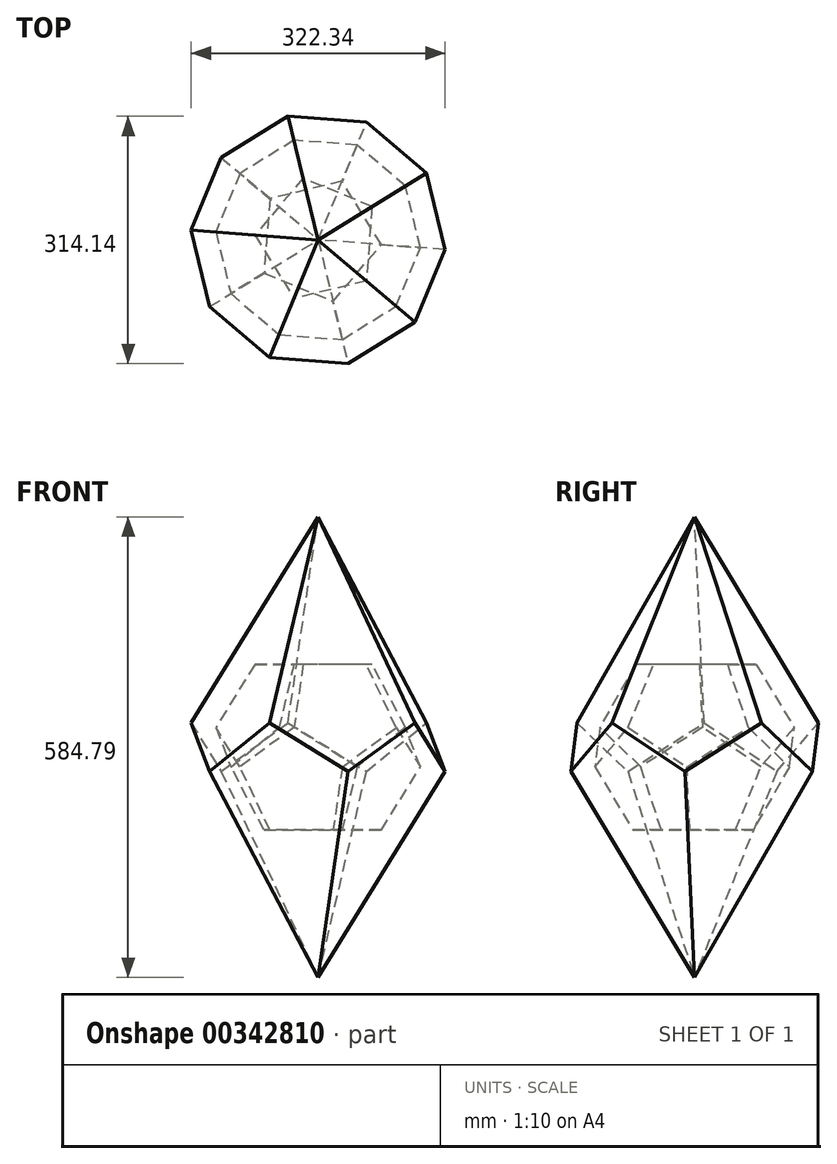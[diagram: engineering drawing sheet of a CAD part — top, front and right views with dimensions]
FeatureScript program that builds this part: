
annotation { "Feature Type Name" : "Feature", "Feature Type Description" : "" }
export const myFeature = defineFeature(function(context is Context, id is Id, definition is map)
    precondition{}
    {
        {
            var Q0;
            Q0=qCreatedBy(makeId("Top.planeOp"),FACE);
            var sketch = newSketch(context, id + "F0", { "sketchPlane" : qUnion([Q0])});
            skCircle(sketch, "E0.cCircle", {"center": v(0, 0) * mm, "radius": 80.82 * mm, "construction": true});
            skLineSegment(sketch, "E0.0", {"start": v(99.6, -7.58) * mm, "end": v(23.57, -97.07) * mm});
            skLineSegment(sketch, "E0.1", {"start": v(23.57, -97.07) * mm, "end": v(-85.04, -52.42) * mm});
            skLineSegment(sketch, "E0.2", {"start": v(-85.04, -52.42) * mm, "end": v(-76.13, 64.68) * mm});
            skLineSegment(sketch, "E0.3", {"start": v(-76.13, 64.68) * mm, "end": v(37.99, 92.39) * mm});
            skLineSegment(sketch, "E0.4", {"start": v(37.99, 92.39) * mm, "end": v(99.6, -7.58) * mm});
            skPoint(sketch, "E0.0.midPoint", {"position": v(61.59, -52.33) * mm});
            skSolve(sketch);
        }
        {
            var Q0;
            Q0=makeQuery(id+"F0.imprint","IMPRINT",FACE,{"disambiguationData":[TD([[makeQuery(id+"F0.imprint","IMPRINT",EDGE,{"derivedFrom":sQuery(id+"F0.wireOp",EDGE,"E0.0")}),-1.0]])]});
            extrude(context, id + "F1", {"entities" : qUnion([Q0]), "depth" : 25.4 * mm});
        }
        {
            var Q0;
            Q0=makeQuery(id+"F1.opExtrude","CAP_EDGE",EDGE,{"disambiguationData":[OSD([sQuery(id+"F0.wireOp",EDGE,"E0.1")])],"isStart":false});
            var Q1;
            Q1=makeQuery(id+"F1.opExtrude","CAP_EDGE",EDGE,{"disambiguationData":[OSD([sQuery(id+"F0.wireOp",EDGE,"E0.2")])],"isStart":false});
            var Q2;
            Q2=makeQuery(id+"F1.opExtrude","CAP_EDGE",EDGE,{"disambiguationData":[OSD([sQuery(id+"F0.wireOp",EDGE,"E0.3")])],"isStart":false});
            var Q3;
            Q3=makeQuery(id+"F1.opExtrude","CAP_EDGE",EDGE,{"disambiguationData":[OSD([sQuery(id+"F0.wireOp",EDGE,"E0.4")])],"isStart":false});
            var Q4;
            Q4=makeQuery(id+"F1.opExtrude","CAP_EDGE",EDGE,{"disambiguationData":[OSD([sQuery(id+"F0.wireOp",EDGE,"E0.0")])],"isStart":false});
            chamfer(context, id + "F2", {"entities" : qUnion([Q0, Q1, Q2, Q3, Q4]), "chamferType" : ChamferType.OFFSET_ANGLE, "width" : 25.4 * mm, "oppositeDirection" : false, "angle" : 31.72 * degree, "tangentPropagation" : true});
        }
        {
            var Q0;
            Q0=makeQuery(id+"F1.opExtrude","SWEPT_BODY",BODY,{"disambiguationData":[OSD([sQuery(id+"F0.wireOp",EDGE,"E0.0"),sQuery(id+"F0.wireOp",EDGE,"E0.1"),sQuery(id+"F0.wireOp",EDGE,"E0.2"),sQuery(id+"F0.wireOp",EDGE,"E0.3"),sQuery(id+"F0.wireOp",EDGE,"E0.4")])]});
            var Q1;
            Q1=makeQuery(id+"F2.opChamfer","BLEND_EDGE",EDGE,{"blendedFrom":[makeQuery(id+"F1.opExtrude","CAP_EDGE",EDGE,{"disambiguationData":[OSD([sQuery(id+"F0.wireOp",EDGE,"E0.1")])],"isStart":false}),makeQuery(id+"F1.opExtrude","CAP_EDGE",EDGE,{"disambiguationData":[OSD([sQuery(id+"F0.wireOp",EDGE,"E0.2")])],"isStart":false})],"blendedInto":[]});
            circularPattern(context, id + "F3", {"entities" : qUnion([Q0]), "axis" : qUnion([Q1]), "angle" : 360 * degree, "instanceCount" : 3, "equalSpace" : true});
        }
        {
            var Q0;
            Q0=makeQuery(id+"F1.opExtrude","SWEPT_BODY",BODY,{"disambiguationData":[OSD([sQuery(id+"F0.wireOp",EDGE,"E0.0"),sQuery(id+"F0.wireOp",EDGE,"E0.1"),sQuery(id+"F0.wireOp",EDGE,"E0.2"),sQuery(id+"F0.wireOp",EDGE,"E0.3"),sQuery(id+"F0.wireOp",EDGE,"E0.4")])]});
            var Q1;
            Q1=makeQuery(id+"F3.opPattern","COPY",BODY,{"derivedFrom":makeQuery(id+"F1.opExtrude","SWEPT_BODY",BODY,{"disambiguationData":[OSD([sQuery(id+"F0.wireOp",EDGE,"E0.0"),sQuery(id+"F0.wireOp",EDGE,"E0.1"),sQuery(id+"F0.wireOp",EDGE,"E0.2"),sQuery(id+"F0.wireOp",EDGE,"E0.3"),sQuery(id+"F0.wireOp",EDGE,"E0.4")])]}),"instanceName":"1"});
            var Q2;
            Q2=makeQuery(id+"F3.opPattern","COPY",BODY,{"derivedFrom":makeQuery(id+"F1.opExtrude","SWEPT_BODY",BODY,{"disambiguationData":[OSD([sQuery(id+"F0.wireOp",EDGE,"E0.0"),sQuery(id+"F0.wireOp",EDGE,"E0.1"),sQuery(id+"F0.wireOp",EDGE,"E0.2"),sQuery(id+"F0.wireOp",EDGE,"E0.3"),sQuery(id+"F0.wireOp",EDGE,"E0.4")])]}),"instanceName":"2"});
            var Q3;
            Q3=makeQuery(id+"F2.opChamfer","BLEND_EDGE",EDGE,{"blendedFrom":[makeQuery(id+"F1.opExtrude","CAP_EDGE",EDGE,{"disambiguationData":[OSD([sQuery(id+"F0.wireOp",EDGE,"E0.0")])],"isStart":false}),makeQuery(id+"F1.opExtrude","CAP_EDGE",EDGE,{"disambiguationData":[OSD([sQuery(id+"F0.wireOp",EDGE,"E0.4")])],"isStart":false})],"blendedInto":[]});
            transform(context, id + "F4", {"entities" : qUnion([Q0, Q1, Q2]), "transformType" : TransformType.ROTATION, "transformAxis" : qUnion([Q3]), "angle" : 120 * degree, "makeCopy" : true});
        }
        {
            var Q0;
            Q0=makeQuery(id+"F4.opPattern","COPY",BODY,{"derivedFrom":makeQuery(id+"F3.opPattern","COPY",BODY,{"derivedFrom":makeQuery(id+"F1.opExtrude","SWEPT_BODY",BODY,{"disambiguationData":[OSD([sQuery(id+"F0.wireOp",EDGE,"E0.0"),sQuery(id+"F0.wireOp",EDGE,"E0.1"),sQuery(id+"F0.wireOp",EDGE,"E0.2"),sQuery(id+"F0.wireOp",EDGE,"E0.3"),sQuery(id+"F0.wireOp",EDGE,"E0.4")])]}),"instanceName":"1"}),"instanceName":"1"});
            var Q1;
            Q1=makeQuery(id+"F4.opPattern","COPY",BODY,{"derivedFrom":makeQuery(id+"F3.opPattern","COPY",BODY,{"derivedFrom":makeQuery(id+"F1.opExtrude","SWEPT_BODY",BODY,{"disambiguationData":[OSD([sQuery(id+"F0.wireOp",EDGE,"E0.0"),sQuery(id+"F0.wireOp",EDGE,"E0.1"),sQuery(id+"F0.wireOp",EDGE,"E0.2"),sQuery(id+"F0.wireOp",EDGE,"E0.3"),sQuery(id+"F0.wireOp",EDGE,"E0.4")])]}),"instanceName":"2"}),"instanceName":"1"});
            var Q2;
            Q2=makeQuery(id+"F4.opPattern","COPY",BODY,{"derivedFrom":makeQuery(id+"F1.opExtrude","SWEPT_BODY",BODY,{"disambiguationData":[OSD([sQuery(id+"F0.wireOp",EDGE,"E0.0"),sQuery(id+"F0.wireOp",EDGE,"E0.1"),sQuery(id+"F0.wireOp",EDGE,"E0.2"),sQuery(id+"F0.wireOp",EDGE,"E0.3"),sQuery(id+"F0.wireOp",EDGE,"E0.4")])]}),"instanceName":"1"});
            var Q3;
            Q3=makeQuery(id+"F4.opPattern","COPY",EDGE,{"derivedFrom":makeQuery(id+"F3.opPattern","COPY",EDGE,{"derivedFrom":makeQuery(id+"F2.opChamfer","BLEND_EDGE",EDGE,{"blendedFrom":[makeQuery(id+"F1.opExtrude","CAP_EDGE",EDGE,{"disambiguationData":[OSD([sQuery(id+"F0.wireOp",EDGE,"E0.0")])],"isStart":false}),makeQuery(id+"F1.opExtrude","CAP_EDGE",EDGE,{"disambiguationData":[OSD([sQuery(id+"F0.wireOp",EDGE,"E0.4")])],"isStart":false})],"blendedInto":[]}),"instanceName":"2"}),"instanceName":"1"});
            transform(context, id + "F5", {"entities" : qUnion([Q0, Q1, Q2]), "transformType" : TransformType.ROTATION, "transformAxis" : qUnion([Q3]), "angle" : 120 * degree, "makeCopy" : true});
        }
        {
            var Q0;
            Q0=makeQuery(id+"F5.opPattern","COPY",BODY,{"derivedFrom":makeQuery(id+"F4.opPattern","COPY",BODY,{"derivedFrom":makeQuery(id+"F1.opExtrude","SWEPT_BODY",BODY,{"disambiguationData":[OSD([sQuery(id+"F0.wireOp",EDGE,"E0.0"),sQuery(id+"F0.wireOp",EDGE,"E0.1"),sQuery(id+"F0.wireOp",EDGE,"E0.2"),sQuery(id+"F0.wireOp",EDGE,"E0.3"),sQuery(id+"F0.wireOp",EDGE,"E0.4")])]}),"instanceName":"1"}),"instanceName":"1"});
            var Q1;
            Q1=makeQuery(id+"F4.opPattern","COPY",BODY,{"derivedFrom":makeQuery(id+"F3.opPattern","COPY",BODY,{"derivedFrom":makeQuery(id+"F1.opExtrude","SWEPT_BODY",BODY,{"disambiguationData":[OSD([sQuery(id+"F0.wireOp",EDGE,"E0.0"),sQuery(id+"F0.wireOp",EDGE,"E0.1"),sQuery(id+"F0.wireOp",EDGE,"E0.2"),sQuery(id+"F0.wireOp",EDGE,"E0.3"),sQuery(id+"F0.wireOp",EDGE,"E0.4")])]}),"instanceName":"2"}),"instanceName":"1"});
            var Q2;
            Q2=makeQuery(id+"F5.opPattern","COPY",BODY,{"derivedFrom":makeQuery(id+"F4.opPattern","COPY",BODY,{"derivedFrom":makeQuery(id+"F3.opPattern","COPY",BODY,{"derivedFrom":makeQuery(id+"F1.opExtrude","SWEPT_BODY",BODY,{"disambiguationData":[OSD([sQuery(id+"F0.wireOp",EDGE,"E0.0"),sQuery(id+"F0.wireOp",EDGE,"E0.1"),sQuery(id+"F0.wireOp",EDGE,"E0.2"),sQuery(id+"F0.wireOp",EDGE,"E0.3"),sQuery(id+"F0.wireOp",EDGE,"E0.4")])]}),"instanceName":"2"}),"instanceName":"1"}),"instanceName":"1"});
            var Q3;
            Q3=makeQuery(id+"F5.opPattern","COPY",EDGE,{"derivedFrom":makeQuery(id+"F4.opPattern","COPY",EDGE,{"derivedFrom":makeQuery(id+"F3.opPattern","COPY",EDGE,{"derivedFrom":makeQuery(id+"F2.opChamfer","BLEND_EDGE",EDGE,{"blendedFrom":[makeQuery(id+"F1.opExtrude","CAP_EDGE",EDGE,{"disambiguationData":[OSD([sQuery(id+"F0.wireOp",EDGE,"E0.2")])],"isStart":false}),makeQuery(id+"F1.opExtrude","CAP_EDGE",EDGE,{"disambiguationData":[OSD([sQuery(id+"F0.wireOp",EDGE,"E0.3")])],"isStart":false})],"blendedInto":[]}),"instanceName":"2"}),"instanceName":"1"}),"instanceName":"1"});
            transform(context, id + "F6", {"entities" : qUnion([Q0, Q1, Q2]), "transformType" : TransformType.ROTATION, "transformAxis" : qUnion([Q3]), "angle" : 240 * degree, "makeCopy" : true});
        }
        {
            var Q0;
            Q0=makeQuery(id+"F6.opPattern","COPY",FACE,{"derivedFrom":makeQuery(id+"F5.opPattern","COPY",FACE,{"derivedFrom":makeQuery(id+"F4.opPattern","COPY",FACE,{"derivedFrom":makeQuery(id+"F3.opPattern","COPY",FACE,{"derivedFrom":makeQuery(id+"F1.opExtrude","CAP_FACE",FACE,{"disambiguationData":[OSD([sQuery(id+"F0.wireOp",EDGE,"E0.0"),sQuery(id+"F0.wireOp",EDGE,"E0.1"),sQuery(id+"F0.wireOp",EDGE,"E0.2"),sQuery(id+"F0.wireOp",EDGE,"E0.3"),sQuery(id+"F0.wireOp",EDGE,"E0.4")])],"isStart":true}),"instanceName":"2"}),"instanceName":"1"}),"instanceName":"1"}),"instanceName":"1"});
            var sketch = newSketch(context, id + "F7", { "sketchPlane" : qUnion([Q0])});
            skLineSegment(sketch, "E1", {"start": v(-103.74, 75.33) * mm, "end": v(-29.05, 432.82) * mm});
            skSolve(sketch);
        }
        {
            var Q0;
            Q0=makeQuery(id+"F6.opPattern","COPY",FACE,{"derivedFrom":makeQuery(id+"F5.opPattern","COPY",FACE,{"derivedFrom":makeQuery(id+"F4.opPattern","COPY",FACE,{"derivedFrom":makeQuery(id+"F1.opExtrude","CAP_FACE",FACE,{"disambiguationData":[OSD([sQuery(id+"F0.wireOp",EDGE,"E0.0"),sQuery(id+"F0.wireOp",EDGE,"E0.1"),sQuery(id+"F0.wireOp",EDGE,"E0.2"),sQuery(id+"F0.wireOp",EDGE,"E0.3"),sQuery(id+"F0.wireOp",EDGE,"E0.4")])],"isStart":true}),"instanceName":"1"}),"instanceName":"1"}),"instanceName":"1"});
            var sketch = newSketch(context, id + "F8", { "sketchPlane" : qUnion([Q0])});
            skLineSegment(sketch, "E2", {"start": v(97.88, 82.8) * mm, "end": v(-27.14, 517.31) * mm});
            skSolve(sketch);
        }
        {
            var Q0;
            {var subQ0=sQuery(id+"F0.wireOp",EDGE,"E0.4");var subQ1=sQuery(id+"F0.wireOp",EDGE,"E0.2");var subQ2=sQuery(id+"F0.wireOp",EDGE,"E0.1");var subQ3=sQuery(id+"F0.wireOp",EDGE,"E0.0");var subQ4=makeQuery(id+"F1.opExtrude","CAP_FACE",FACE,{"disambiguationData":[OSD([subQ3,subQ2,subQ1,sQuery(id+"F0.wireOp",EDGE,"E0.3"),subQ0])],"isStart":true});Q0=makeQuery(id+"F7.imprint","IMPRINT",FACE,{"disambiguationData":[TD([[makeQuery(id+"F7.imprint","IMPRINT",EDGE,{"derivedFrom":makeQuery(id+"F6.opPattern","COPY",EDGE,{"derivedFrom":makeQuery(id+"F5.opPattern","COPY",EDGE,{"derivedFrom":makeQuery(id+"F4.opPattern","COPY",EDGE,{"derivedFrom":makeQuery(id+"F3.opPattern","COPY",EDGE,{"derivedFrom":makeQuery(id+"F2.opChamfer","BLEND_EDGE",EDGE,{"blendedFrom":[makeQuery(id+"F1.opExtrude","CAP_EDGE",EDGE,{"disambiguationData":[OSD([subQ3])],"isStart":false}),subQ4],"blendedInto":[subQ4]}),"instanceName":"2"}),"instanceName":"1"}),"instanceName":"1"}),"instanceName":"1"})}),1.0]])]});}
            var sketch = newSketch(context, id + "F9", { "sketchPlane" : qUnion([Q0])});
            skLineSegment(sketch, "E3", {"start": v(-40.86, 376.27) * mm, "end": v(-0.97, 360.76) * mm});
            skSolve(sketch);
        }
        {
            var Q1;
            Q1=makeQuery(id+"F5.opPattern","COPY",FACE,{"derivedFrom":makeQuery(id+"F4.opPattern","COPY",FACE,{"derivedFrom":makeQuery(id+"F3.opPattern","COPY",FACE,{"derivedFrom":makeQuery(id+"F1.opExtrude","CAP_FACE",FACE,{"disambiguationData":[OSD([sQuery(id+"F0.wireOp",EDGE,"E0.0"),sQuery(id+"F0.wireOp",EDGE,"E0.1"),sQuery(id+"F0.wireOp",EDGE,"E0.2"),sQuery(id+"F0.wireOp",EDGE,"E0.3"),sQuery(id+"F0.wireOp",EDGE,"E0.4")])],"isStart":true}),"instanceName":"2"}),"instanceName":"1"}),"instanceName":"1"});
            var Q2;
            Q2=sQuery(id+"F9.wireOp",VERTEX,"E3.start");
            loft(context, id + "F10", {"operationType" : NewBodyOperationType.ADD, "sheetProfilesArray" : [{ "sheetProfileEntities" : qUnion([Q1]) }, { "sheetProfileEntities" : qUnion([Q2]) }]});
        }
        {
            var Q0;
            Q0=makeQuery(id+"F6.opPattern","COPY",FACE,{"derivedFrom":makeQuery(id+"F4.opPattern","COPY",FACE,{"derivedFrom":makeQuery(id+"F3.opPattern","COPY",FACE,{"derivedFrom":makeQuery(id+"F1.opExtrude","CAP_FACE",FACE,{"disambiguationData":[OSD([sQuery(id+"F0.wireOp",EDGE,"E0.0"),sQuery(id+"F0.wireOp",EDGE,"E0.1"),sQuery(id+"F0.wireOp",EDGE,"E0.2"),sQuery(id+"F0.wireOp",EDGE,"E0.3"),sQuery(id+"F0.wireOp",EDGE,"E0.4")])],"isStart":true}),"instanceName":"2"}),"instanceName":"1"}),"instanceName":"1"});
            var sketch = newSketch(context, id + "F11", { "sketchPlane" : qUnion([Q0])});
            skLineSegment(sketch, "E4", {"start": v(38.24, 132.45) * mm, "end": v(57.54, -261.56) * mm});
            skSolve(sketch);
        }
        {
            var Q0;
            Q0=makeQuery(id+"F3.opPattern","COPY",FACE,{"derivedFrom":makeQuery(id+"F1.opExtrude","CAP_FACE",FACE,{"disambiguationData":[OSD([sQuery(id+"F0.wireOp",EDGE,"E0.0"),sQuery(id+"F0.wireOp",EDGE,"E0.1"),sQuery(id+"F0.wireOp",EDGE,"E0.2"),sQuery(id+"F0.wireOp",EDGE,"E0.3"),sQuery(id+"F0.wireOp",EDGE,"E0.4")])],"isStart":true}),"instanceName":"1"});
            var sketch = newSketch(context, id + "F12", { "sketchPlane" : qUnion([Q0])});
            skLineSegment(sketch, "E5", {"start": v(63.3, 137.03) * mm, "end": v(11.57, -251.7) * mm});
            skLineSegment(sketch, "E6", {"start": v(-108.02, 105.75) * mm, "end": v(104.5, -286.97) * mm});
            skLineSegment(sketch, "E7", {"start": v(-9.37, -80.49) * mm, "end": v(26.14, -142.18) * mm});
            skSolve(sketch);
        }
        {
            var Q1;
            Q1=makeQuery(id+"F1.opExtrude","CAP_FACE",FACE,{"disambiguationData":[OSD([sQuery(id+"F0.wireOp",EDGE,"E0.0"),sQuery(id+"F0.wireOp",EDGE,"E0.1"),sQuery(id+"F0.wireOp",EDGE,"E0.2"),sQuery(id+"F0.wireOp",EDGE,"E0.3"),sQuery(id+"F0.wireOp",EDGE,"E0.4")])],"isStart":true});
            var Q2;
            Q2=sQuery(id+"F12.wireOp",VERTEX,"E7.end");
            loft(context, id + "F13", {"operationType" : NewBodyOperationType.ADD, "sheetProfilesArray" : [{ "sheetProfileEntities" : qUnion([Q1]) }, { "sheetProfileEntities" : qUnion([Q2]) }]});
        }
        {
            var Q0;
            Q0=makeQuery(id+"F1.opExtrude","SWEPT_BODY",BODY,{"disambiguationData":[OSD([sQuery(id+"F0.wireOp",EDGE,"E0.0"),sQuery(id+"F0.wireOp",EDGE,"E0.1"),sQuery(id+"F0.wireOp",EDGE,"E0.2"),sQuery(id+"F0.wireOp",EDGE,"E0.3"),sQuery(id+"F0.wireOp",EDGE,"E0.4")])]});
            var Q1;
            Q1=makeQuery(id+"F4.opPattern","COPY",BODY,{"derivedFrom":makeQuery(id+"F1.opExtrude","SWEPT_BODY",BODY,{"disambiguationData":[OSD([sQuery(id+"F0.wireOp",EDGE,"E0.0"),sQuery(id+"F0.wireOp",EDGE,"E0.1"),sQuery(id+"F0.wireOp",EDGE,"E0.2"),sQuery(id+"F0.wireOp",EDGE,"E0.3"),sQuery(id+"F0.wireOp",EDGE,"E0.4")])]}),"instanceName":"1"});
            var Q2;
            Q2=makeQuery(id+"F6.opPattern","COPY",BODY,{"derivedFrom":makeQuery(id+"F4.opPattern","COPY",BODY,{"derivedFrom":makeQuery(id+"F3.opPattern","COPY",BODY,{"derivedFrom":makeQuery(id+"F1.opExtrude","SWEPT_BODY",BODY,{"disambiguationData":[OSD([sQuery(id+"F0.wireOp",EDGE,"E0.0"),sQuery(id+"F0.wireOp",EDGE,"E0.1"),sQuery(id+"F0.wireOp",EDGE,"E0.2"),sQuery(id+"F0.wireOp",EDGE,"E0.3"),sQuery(id+"F0.wireOp",EDGE,"E0.4")])]}),"instanceName":"2"}),"instanceName":"1"}),"instanceName":"1"});
            var Q3;
            Q3=makeQuery(id+"F3.opPattern","COPY",BODY,{"derivedFrom":makeQuery(id+"F1.opExtrude","SWEPT_BODY",BODY,{"disambiguationData":[OSD([sQuery(id+"F0.wireOp",EDGE,"E0.0"),sQuery(id+"F0.wireOp",EDGE,"E0.1"),sQuery(id+"F0.wireOp",EDGE,"E0.2"),sQuery(id+"F0.wireOp",EDGE,"E0.3"),sQuery(id+"F0.wireOp",EDGE,"E0.4")])]}),"instanceName":"1"});
            var Q4;
            Q4=makeQuery(id+"F6.opPattern","COPY",BODY,{"derivedFrom":makeQuery(id+"F5.opPattern","COPY",BODY,{"derivedFrom":makeQuery(id+"F4.opPattern","COPY",BODY,{"derivedFrom":makeQuery(id+"F1.opExtrude","SWEPT_BODY",BODY,{"disambiguationData":[OSD([sQuery(id+"F0.wireOp",EDGE,"E0.0"),sQuery(id+"F0.wireOp",EDGE,"E0.1"),sQuery(id+"F0.wireOp",EDGE,"E0.2"),sQuery(id+"F0.wireOp",EDGE,"E0.3"),sQuery(id+"F0.wireOp",EDGE,"E0.4")])]}),"instanceName":"1"}),"instanceName":"1"}),"instanceName":"1"});
            var Q5;
            Q5=makeQuery(id+"F6.opPattern","COPY",BODY,{"derivedFrom":makeQuery(id+"F5.opPattern","COPY",BODY,{"derivedFrom":makeQuery(id+"F4.opPattern","COPY",BODY,{"derivedFrom":makeQuery(id+"F3.opPattern","COPY",BODY,{"derivedFrom":makeQuery(id+"F1.opExtrude","SWEPT_BODY",BODY,{"disambiguationData":[OSD([sQuery(id+"F0.wireOp",EDGE,"E0.0"),sQuery(id+"F0.wireOp",EDGE,"E0.1"),sQuery(id+"F0.wireOp",EDGE,"E0.2"),sQuery(id+"F0.wireOp",EDGE,"E0.3"),sQuery(id+"F0.wireOp",EDGE,"E0.4")])]}),"instanceName":"2"}),"instanceName":"1"}),"instanceName":"1"}),"instanceName":"1"});
            var Q6;
            Q6=makeQuery(id+"F5.opPattern","COPY",BODY,{"derivedFrom":makeQuery(id+"F4.opPattern","COPY",BODY,{"derivedFrom":makeQuery(id+"F3.opPattern","COPY",BODY,{"derivedFrom":makeQuery(id+"F1.opExtrude","SWEPT_BODY",BODY,{"disambiguationData":[OSD([sQuery(id+"F0.wireOp",EDGE,"E0.0"),sQuery(id+"F0.wireOp",EDGE,"E0.1"),sQuery(id+"F0.wireOp",EDGE,"E0.2"),sQuery(id+"F0.wireOp",EDGE,"E0.3"),sQuery(id+"F0.wireOp",EDGE,"E0.4")])]}),"instanceName":"2"}),"instanceName":"1"}),"instanceName":"1"});
            var Q7;
            Q7=makeQuery(id+"F5.opPattern","COPY",BODY,{"derivedFrom":makeQuery(id+"F4.opPattern","COPY",BODY,{"derivedFrom":makeQuery(id+"F1.opExtrude","SWEPT_BODY",BODY,{"disambiguationData":[OSD([sQuery(id+"F0.wireOp",EDGE,"E0.0"),sQuery(id+"F0.wireOp",EDGE,"E0.1"),sQuery(id+"F0.wireOp",EDGE,"E0.2"),sQuery(id+"F0.wireOp",EDGE,"E0.3"),sQuery(id+"F0.wireOp",EDGE,"E0.4")])]}),"instanceName":"1"}),"instanceName":"1"});
            var Q8;
            Q8=makeQuery(id+"F4.opPattern","COPY",BODY,{"derivedFrom":makeQuery(id+"F3.opPattern","COPY",BODY,{"derivedFrom":makeQuery(id+"F1.opExtrude","SWEPT_BODY",BODY,{"disambiguationData":[OSD([sQuery(id+"F0.wireOp",EDGE,"E0.0"),sQuery(id+"F0.wireOp",EDGE,"E0.1"),sQuery(id+"F0.wireOp",EDGE,"E0.2"),sQuery(id+"F0.wireOp",EDGE,"E0.3"),sQuery(id+"F0.wireOp",EDGE,"E0.4")])]}),"instanceName":"2"}),"instanceName":"1"});
            var Q9;
            Q9=makeQuery(id+"F4.opPattern","COPY",BODY,{"derivedFrom":makeQuery(id+"F3.opPattern","COPY",BODY,{"derivedFrom":makeQuery(id+"F1.opExtrude","SWEPT_BODY",BODY,{"disambiguationData":[OSD([sQuery(id+"F0.wireOp",EDGE,"E0.0"),sQuery(id+"F0.wireOp",EDGE,"E0.1"),sQuery(id+"F0.wireOp",EDGE,"E0.2"),sQuery(id+"F0.wireOp",EDGE,"E0.3"),sQuery(id+"F0.wireOp",EDGE,"E0.4")])]}),"instanceName":"1"}),"instanceName":"1"});
            var Q10;
            Q10=makeQuery(id+"F3.opPattern","COPY",BODY,{"derivedFrom":makeQuery(id+"F1.opExtrude","SWEPT_BODY",BODY,{"disambiguationData":[OSD([sQuery(id+"F0.wireOp",EDGE,"E0.0"),sQuery(id+"F0.wireOp",EDGE,"E0.1"),sQuery(id+"F0.wireOp",EDGE,"E0.2"),sQuery(id+"F0.wireOp",EDGE,"E0.3"),sQuery(id+"F0.wireOp",EDGE,"E0.4")])]}),"instanceName":"2"});
            var Q11;
            Q11=makeQuery(id+"F5.opPattern","COPY",BODY,{"derivedFrom":makeQuery(id+"F4.opPattern","COPY",BODY,{"derivedFrom":makeQuery(id+"F3.opPattern","COPY",BODY,{"derivedFrom":makeQuery(id+"F1.opExtrude","SWEPT_BODY",BODY,{"disambiguationData":[OSD([sQuery(id+"F0.wireOp",EDGE,"E0.0"),sQuery(id+"F0.wireOp",EDGE,"E0.1"),sQuery(id+"F0.wireOp",EDGE,"E0.2"),sQuery(id+"F0.wireOp",EDGE,"E0.3"),sQuery(id+"F0.wireOp",EDGE,"E0.4")])]}),"instanceName":"1"}),"instanceName":"1"}),"instanceName":"1"});
            booleanBodies(context, id + "F14", {"operationType" : BooleanOperationType.UNION, "tools" : qUnion([Q0, Q1, Q2, Q3, Q4, Q5, Q6, Q7, Q8, Q9, Q10, Q11])});
        }
    });
